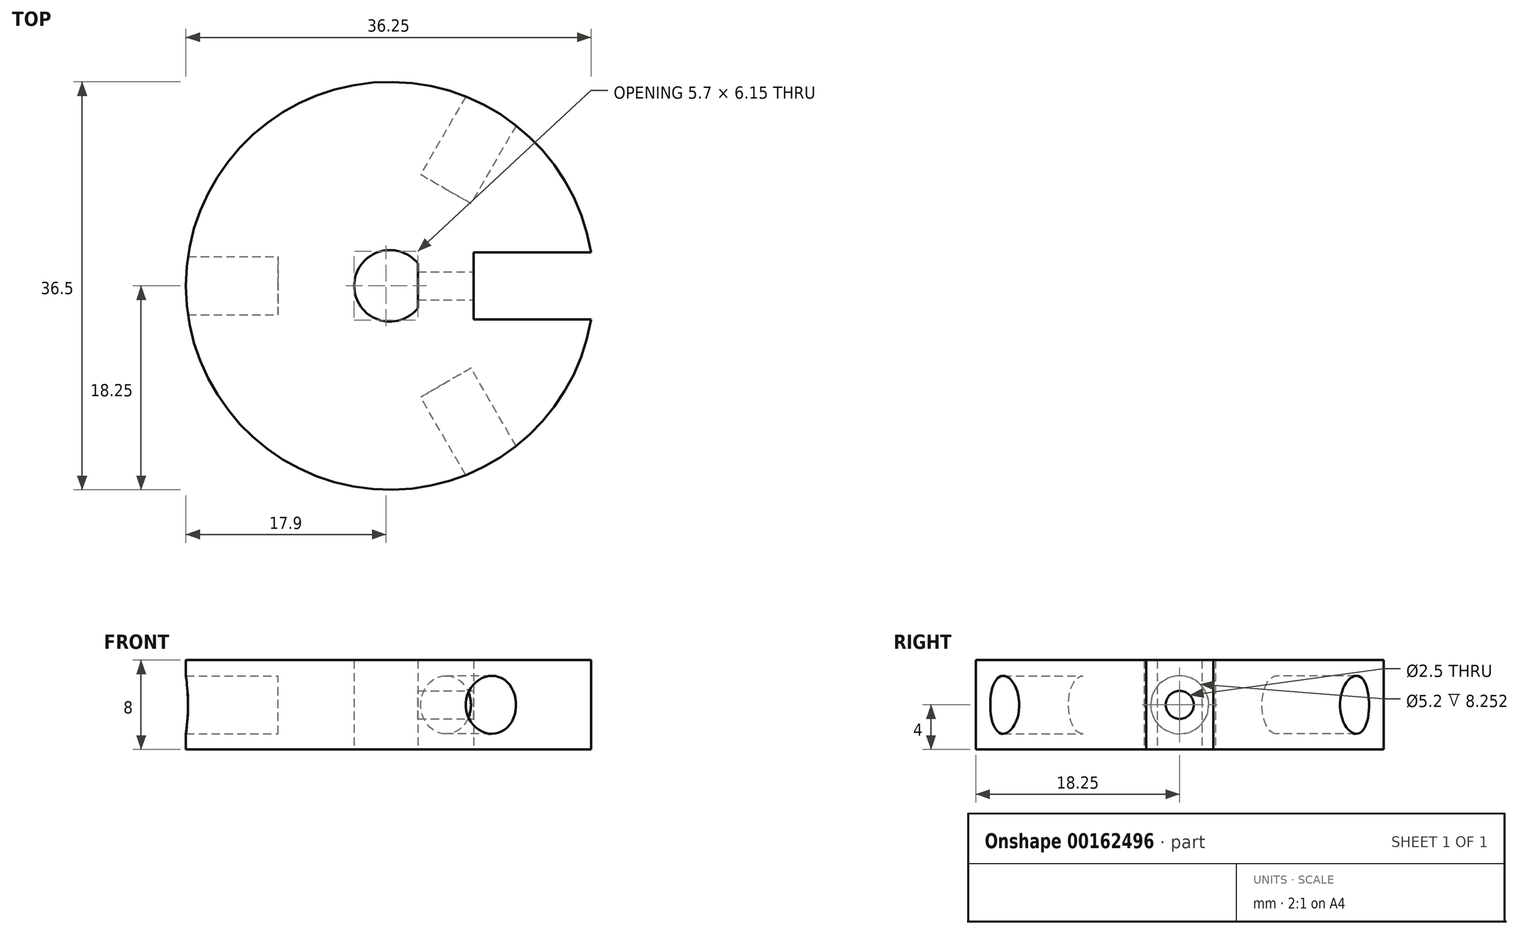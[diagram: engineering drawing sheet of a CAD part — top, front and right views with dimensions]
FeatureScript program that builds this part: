
annotation { "Feature Type Name" : "Feature", "Feature Type Description" : "" }
export const myFeature = defineFeature(function(context is Context, id is Id, definition is map)
    precondition{}
    {
        {
            var Q0;
            Q0=qCreatedBy(makeId("Top.planeOp"),FACE);
            var sketch = newSketch(context, id + "F0", { "sketchPlane" : qUnion([Q0])});
            skArc(sketch, "E0", {"start": v(18, 3) * mm, "mid": v(-18.25, 0) * mm, "end": v(18, -3) * mm});
            skArc(sketch, "E1", {"start": v(2.5, 2) * mm, "mid": v(-3.2, 0) * mm, "end": v(2.5, -2) * mm});
            skLineSegment(sketch, "E2", {"start": v(2.5, 2) * mm, "end": v(2.5, -2) * mm});
            skLineSegment(sketch, "E3", {"start": v(7.5, 0) * mm, "end": v(7.5, 3) * mm});
            skLineSegment(sketch, "E4", {"start": v(7.5, 3) * mm, "end": v(18, 3) * mm});
            skLineSegment(sketch, "E5", {"start": v(0, 0) * mm, "end": v(25.05, 0) * mm, "construction": true});
            skPoint(sketch, "E5.endSnap0", {"position": v(2.5, 0) * mm});
            skLineSegment(sketch, "E6.MirrorCS", {"start": v(7.5, 0) * mm, "end": v(7.5, -3) * mm});
            skLineSegment(sketch, "E7.MirrorCS", {"start": v(7.5, -3) * mm, "end": v(18, -3) * mm});
            skSolve(sketch);
        }
        {
            var Q0;
            Q0 = qSketchRegion(id + "F0", true);
            extrude(context, id + "F1", {"entities" : qUnion([Q0]), "depth" : 8 * mm});
        }
        {
            var Q0;
            Q0=makeQuery(id+"F1.opExtrude","SWEPT_FACE",FACE,{"disambiguationData":[OSD([sQuery(id+"F0.wireOp",EDGE,"E3"),sQuery(id+"F0.wireOp",EDGE,"E6.MirrorCS")])]});
            var sketch = newSketch(context, id + "F2", { "sketchPlane" : qUnion([Q0])});
            skLineSegment(sketch, "E8", {"start": v(3, 4) * mm, "end": v(-3, 4) * mm, "construction": true});
            skCircle(sketch, "E9", {"center": v(0, 4) * mm, "radius": 1.25 * mm});
            skSolve(sketch);
        }
        {
            var Q0;
            Q0 = qSketchRegion(id + "F2", true);
            extrude(context, id + "F3", {"entities" : qUnion([Q0]), "operationType" : NewBodyOperationType.REMOVE, "endBound" : BoundingType.UP_TO_NEXT, "oppositeDirection" : true, "depth" : 25 * mm});
        }
        {
            var Q0;
            Q0=qCreatedBy(makeId("Right.planeOp"),FACE);
            cPlane(context, id + "F4", {"entities" : qUnion([Q0]), "cplaneType" : CPlaneType.OFFSET, "offset" : 10 * mm, "oppositeDirection" : true, "width" : 150 * mm, "height" : 150 * mm});
        }
        {
            var Q0;
            Q0=qCreatedBy(id+"F4.planeOp",FACE);
            var sketch = newSketch(context, id + "F5", { "sketchPlane" : qUnion([Q0])});
            skCircle(sketch, "E10", {"center": v(0, 4) * mm, "radius": 2.6 * mm});
            skSolve(sketch);
        }
        {
            var Q0;
            Q0 = qSketchRegion(id + "F5", true);
            extrude(context, id + "F6", {"entities" : qUnion([Q0]), "oppositeDirection" : true, "depth" : 25 * mm});
        }
        {
            var Q0;
            Q0=makeQuery(id+"F6.opExtrude","SWEPT_BODY",BODY,{"disambiguationData":[OSD([sQuery(id+"F5.wireOp",EDGE,"E10")])]});
            var Q1;
            Q1=makeQuery(id+"F1.opExtrude","SWEPT_FACE",FACE,{"disambiguationData":[OSD([sQuery(id+"F0.wireOp",EDGE,"E0")])]});
            circularPattern(context, id + "F7", {"entities" : qUnion([Q0]), "axis" : qUnion([Q1]), "angle" : 120 * degree, "instanceCount" : 3});
        }
        {
            var Q0;
            Q0=makeQuery(id+"F6.opExtrude","SWEPT_BODY",BODY,{"disambiguationData":[OSD([sQuery(id+"F5.wireOp",EDGE,"E10")])]});
            var Q1;
            Q1=makeQuery(id+"F7.opPattern","COPY",BODY,{"derivedFrom":makeQuery(id+"F6.opExtrude","SWEPT_BODY",BODY,{"disambiguationData":[OSD([sQuery(id+"F5.wireOp",EDGE,"E10")])]}),"instanceName":"1"});
            var Q2;
            Q2=makeQuery(id+"F7.opPattern","COPY",BODY,{"derivedFrom":makeQuery(id+"F6.opExtrude","SWEPT_BODY",BODY,{"disambiguationData":[OSD([sQuery(id+"F5.wireOp",EDGE,"E10")])]}),"instanceName":"2"});
            var Q3;
            Q3=makeQuery(id+"F1.opExtrude","SWEPT_BODY",BODY,{"disambiguationData":[OSD([sQuery(id+"F0.wireOp",EDGE,"E0"),sQuery(id+"F0.wireOp",EDGE,"E1"),sQuery(id+"F0.wireOp",EDGE,"E2"),sQuery(id+"F0.wireOp",EDGE,"E3"),sQuery(id+"F0.wireOp",EDGE,"E4"),sQuery(id+"F0.wireOp",EDGE,"E6.MirrorCS"),sQuery(id+"F0.wireOp",EDGE,"E7.MirrorCS")])]});
            booleanBodies(context, id + "F8", {"operationType" : BooleanOperationType.SUBTRACTION, "tools" : qUnion([Q0, Q1, Q2]), "targets" : qUnion([Q3])});
        }
    });
